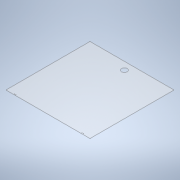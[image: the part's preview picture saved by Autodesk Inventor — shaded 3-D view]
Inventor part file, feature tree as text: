
AUTODESK INVENTOR PART (.ipt)
format: ipt  version: 2022 (Build 260153000, 153)  size: 126,976 bytes
history: native  units: mm
features: sketch x3, hole x2, other x1, extrude x1, fillet x1
ambient origin geometry x8: Origin, YZ Plane, XZ Plane, XY Plane, X Axis, Y Axis, Z Axis, Center Point
bodies: Body1 (feature_tree)
feature tree (8):
  other  "Sólido1"
  extrude  "Extrusão1"  Depth=440.0mm
  hole  "Furo1"  [1 undecoded]
  fillet  "Arredondamento1"  [1 undecoded]
  hole  "Furo2"  [1 undecoded]
  sketch  "Esboço1"  dims[d0=440.0mm d1=440.0mm]
  sketch  "Esboço2"  dims[d2=2.0mm d3=0.0mm]
  sketch  "Esboço3"  dims[d4=2.0mm d5=6.0mm d6=4.0mm d7=2.0mm d8=90.0deg d9=8.0mm d10=20.594885mm d11=2.0mm d12=30.0mm d13=6.0mm d14=4.0mm d15=2.0mm d16=90.0deg d17=8.0mm d18=20.594885mm]
note: 3 required parameter values undecoded (feature->parameter linkage not recoverable at this tier; creation-order binding heuristic only, values carry confidence <= 0.55)
